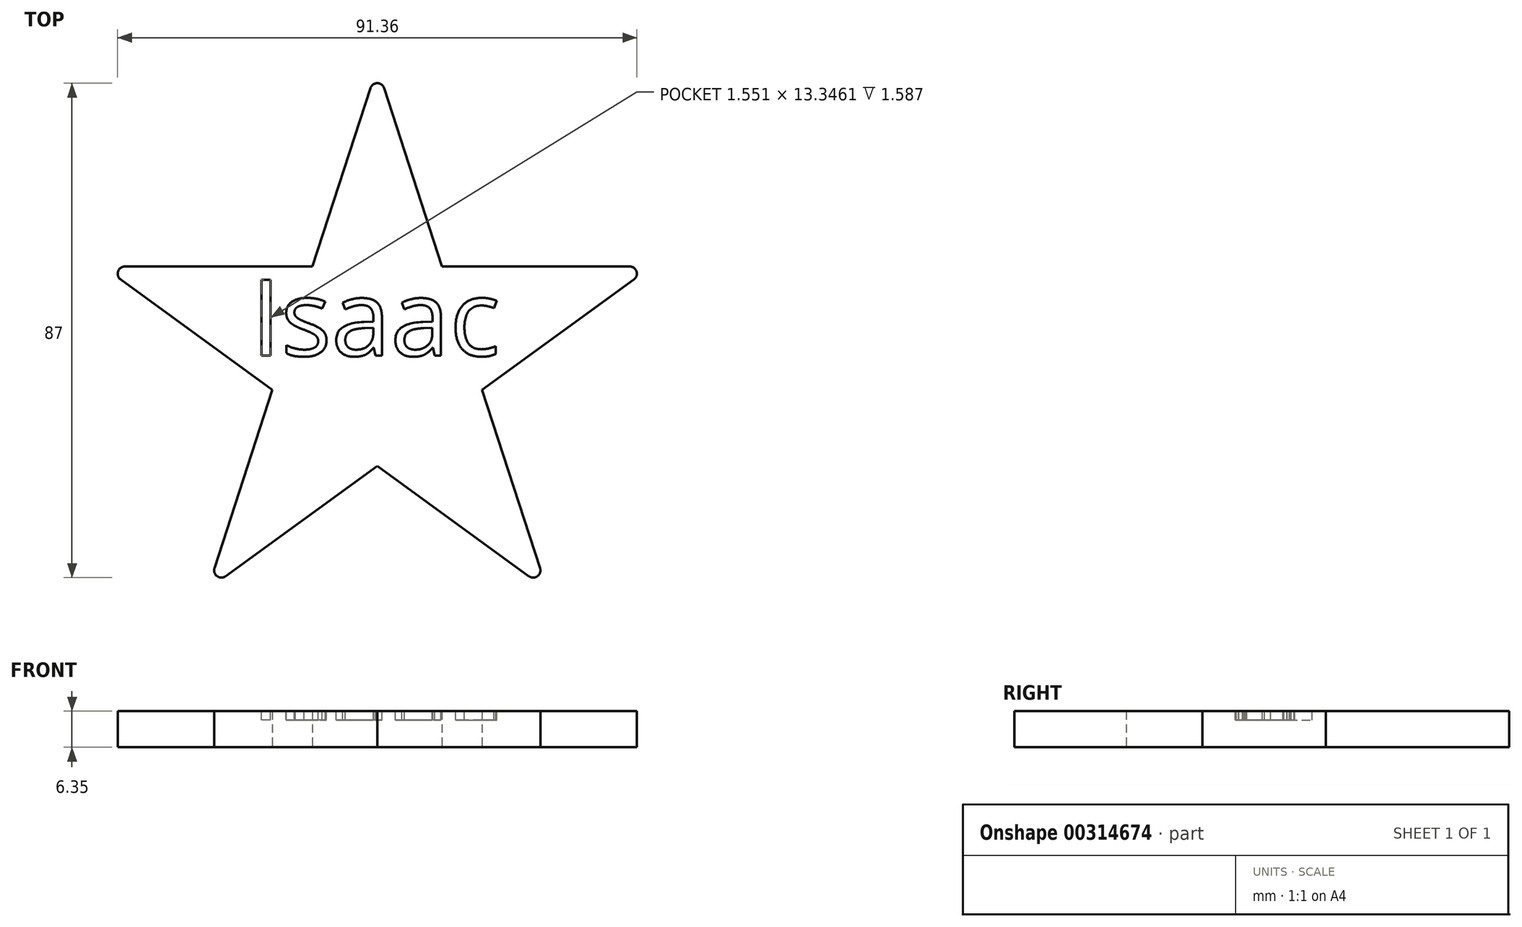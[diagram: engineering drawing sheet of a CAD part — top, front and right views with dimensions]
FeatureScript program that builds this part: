
annotation { "Feature Type Name" : "Feature", "Feature Type Description" : "" }
export const myFeature = defineFeature(function(context is Context, id is Id, definition is map)
    precondition{}
    {
        {
            var Q0;
            Q0=qCreatedBy(makeId("Top.planeOp"),FACE);
            var sketch = newSketch(context, id + "F0", { "sketchPlane" : qUnion([Q0])});
            skCircle(sketch, "E0.cCircle", {"center": v(0, 0) * mm, "radius": 50.8 * mm, "construction": true});
            skLineSegment(sketch, "E0.0", {"start": v(0, 50.8) * mm, "end": v(48.31, 15.7) * mm});
            skLineSegment(sketch, "E0.1", {"start": v(48.31, 15.7) * mm, "end": v(29.86, -41.1) * mm});
            skLineSegment(sketch, "E0.2", {"start": v(29.86, -41.1) * mm, "end": v(-29.86, -41.1) * mm});
            skLineSegment(sketch, "E0.3", {"start": v(-29.86, -41.1) * mm, "end": v(-48.31, 15.7) * mm});
            skLineSegment(sketch, "E0.4", {"start": v(-48.31, 15.7) * mm, "end": v(0, 50.8) * mm});
            skLineSegment(sketch, "E1", {"start": v(0, 50.8) * mm, "end": v(-29.86, -41.1) * mm});
            skLineSegment(sketch, "E2", {"start": v(0, 50.8) * mm, "end": v(29.86, -41.1) * mm});
            skLineSegment(sketch, "E3", {"start": v(-48.31, 15.7) * mm, "end": v(48.31, 15.7) * mm});
            skLineSegment(sketch, "E4", {"start": v(-48.31, 15.7) * mm, "end": v(29.86, -41.1) * mm});
            skLineSegment(sketch, "E5", {"start": v(48.31, 15.7) * mm, "end": v(-29.86, -41.1) * mm});
            skSolve(sketch);
        }
        {
            var Q0;
            {var subQ1=sQuery(id+"F0.wireOp",EDGE,"E1");var subQ3=sQuery(id+"F0.wireOp",EDGE,"E4");var subQ4=makeQuery(id+"F0.imprint","INTERSECT",VERTEX,{"derivedFrom":[subQ1,subQ3]});Q0=makeQuery(id+"F0.imprint","IMPRINT",FACE,{"disambiguationData":[TD([[makeQuery(id+"F0.imprint","IMPRINT",EDGE,{"disambiguationData":[TD([[subQ4,-1.0]])],"derivedFrom":subQ3}),-1.0]])]});}
            var Q1;
            {var subQ0=sQuery(id+"F0.wireOp",EDGE,"E3");var subQ1=sQuery(id+"F0.wireOp",EDGE,"E1");var subQ2=makeQuery(id+"F0.imprint","INTERSECT",VERTEX,{"derivedFrom":[subQ1,subQ0]});Q1=makeQuery(id+"F0.imprint","IMPRINT",FACE,{"disambiguationData":[TD([[makeQuery(id+"F0.imprint","IMPRINT",EDGE,{"disambiguationData":[TD([[subQ2,-1.0]])],"derivedFrom":subQ1}),-1.0]])]});}
            var Q2;
            {var subQ1=sQuery(id+"F0.wireOp",EDGE,"E1");var subQ3=sQuery(id+"F0.wireOp",EDGE,"E3");var subQ4=makeQuery(id+"F0.imprint","INTERSECT",VERTEX,{"derivedFrom":[subQ1,subQ3]});Q2=makeQuery(id+"F0.imprint","IMPRINT",FACE,{"disambiguationData":[TD([[makeQuery(id+"F0.imprint","IMPRINT",EDGE,{"disambiguationData":[TD([[subQ4,-1.0]])],"derivedFrom":subQ3}),1.0]])]});}
            var Q3;
            {var subQ1=sQuery(id+"F0.wireOp",EDGE,"E1");var subQ5=sQuery(id+"F0.wireOp",EDGE,"E3");var subQ6=makeQuery(id+"F0.imprint","INTERSECT",VERTEX,{"derivedFrom":[subQ1,subQ5]});Q3=makeQuery(id+"F0.imprint","IMPRINT",FACE,{"disambiguationData":[TD([[makeQuery(id+"F0.imprint","IMPRINT",EDGE,{"disambiguationData":[TD([[subQ6,-1.0]])],"derivedFrom":subQ1}),1.0]])]});}
            var Q4;
            {var subQ0=sQuery(id+"F0.wireOp",EDGE,"E3");var subQ1=sQuery(id+"F0.wireOp",EDGE,"E2");var subQ2=makeQuery(id+"F0.imprint","INTERSECT",VERTEX,{"derivedFrom":[subQ1,subQ0]});Q4=makeQuery(id+"F0.imprint","IMPRINT",FACE,{"disambiguationData":[TD([[makeQuery(id+"F0.imprint","IMPRINT",EDGE,{"disambiguationData":[TD([[subQ2,-1.0]])],"derivedFrom":subQ1}),1.0]])]});}
            var Q5;
            {var subQ1=sQuery(id+"F0.wireOp",EDGE,"E2");var subQ3=sQuery(id+"F0.wireOp",EDGE,"E5");var subQ4=makeQuery(id+"F0.imprint","INTERSECT",VERTEX,{"derivedFrom":[subQ1,subQ3]});Q5=makeQuery(id+"F0.imprint","IMPRINT",FACE,{"disambiguationData":[TD([[makeQuery(id+"F0.imprint","IMPRINT",EDGE,{"disambiguationData":[TD([[subQ4,-1.0]])],"derivedFrom":subQ3}),1.0]])]});}
            extrude(context, id + "F1", {"entities" : qUnion([Q0, Q1, Q2, Q3, Q4, Q5]), "depth" : 6.35 * mm});
        }
        {
            var Q0;
            Q0=makeQuery(id+"F1.opExtrude","SWEPT_EDGE",EDGE,{"disambiguationData":[OSD([sQuery(id+"F0.wireOp",EDGE,"E0.2"),sQuery(id+"F0.wireOp",EDGE,"E0.3"),sQuery(id+"F0.wireOp",EDGE,"E1"),sQuery(id+"F0.wireOp",EDGE,"E5")])]});
            var Q1;
            Q1=makeQuery(id+"F1.opExtrude","SWEPT_EDGE",EDGE,{"disambiguationData":[OSD([sQuery(id+"F0.wireOp",EDGE,"E0.1"),sQuery(id+"F0.wireOp",EDGE,"E0.2"),sQuery(id+"F0.wireOp",EDGE,"E2"),sQuery(id+"F0.wireOp",EDGE,"E4")])]});
            var Q2;
            Q2=makeQuery(id+"F1.opExtrude","SWEPT_EDGE",EDGE,{"disambiguationData":[OSD([sQuery(id+"F0.wireOp",EDGE,"E0.0"),sQuery(id+"F0.wireOp",EDGE,"E0.1"),sQuery(id+"F0.wireOp",EDGE,"E3"),sQuery(id+"F0.wireOp",EDGE,"E5")])]});
            var Q3;
            Q3=makeQuery(id+"F1.opExtrude","SWEPT_EDGE",EDGE,{"disambiguationData":[OSD([sQuery(id+"F0.wireOp",EDGE,"E0.0"),sQuery(id+"F0.wireOp",EDGE,"E0.4"),sQuery(id+"F0.wireOp",EDGE,"E1"),sQuery(id+"F0.wireOp",EDGE,"E2")])]});
            var Q4;
            Q4=makeQuery(id+"F1.opExtrude","SWEPT_EDGE",EDGE,{"disambiguationData":[OSD([sQuery(id+"F0.wireOp",EDGE,"E0.3"),sQuery(id+"F0.wireOp",EDGE,"E0.4"),sQuery(id+"F0.wireOp",EDGE,"E3"),sQuery(id+"F0.wireOp",EDGE,"E4")])]});
            fillet(context, id + "F2", {"entities" : qUnion([Q0, Q1, Q2, Q3, Q4]), "radius" : 1.27 * mm, "tangentPropagation" : true, "allowEdgeOverflow" : false});
        }
        {
            var Q0;
            Q0=makeQuery(id+"F1.opExtrude","CAP_FACE",FACE,{"disambiguationData":[OSD([sQuery(id+"F0.wireOp",EDGE,"E1"),sQuery(id+"F0.wireOp",EDGE,"E2"),sQuery(id+"F0.wireOp",EDGE,"E3"),sQuery(id+"F0.wireOp",EDGE,"E4"),sQuery(id+"F0.wireOp",EDGE,"E5")])],"isStart":false});
            var sketch = newSketch(context, id + "F3", { "sketchPlane" : qUnion([Q0])});
            skText(sketch, "E6", { "text": "Isaac", "fontName": "OpenSans-Regular.ttf"});
            const initialGuessF3  = {"E6": [-0.0222, 0, 1, 0, 0.01346]};
            skSetInitialGuess(sketch, initialGuessF3);
            skSolve(sketch);
        }
        {
            var Q0;
            Q0=makeQuery(id+"F3.imprint","IMPRINT",FACE,{"disambiguationData":[TD([[makeQuery(id+"F3.imprint","IMPRINT",EDGE,{"derivedFrom":sQuery(id+"F3.wireOp",EDGE,"E6.sketch_text.stroke-29")}),-1.0]])]});
            var Q1;
            Q1=makeQuery(id+"F3.imprint","IMPRINT",FACE,{"disambiguationData":[TD([[makeQuery(id+"F3.imprint","IMPRINT",EDGE,{"derivedFrom":sQuery(id+"F3.wireOp",EDGE,"E6.sketch_text.stroke-4")}),-1.0]])]});
            var Q2;
            Q2=makeQuery(id+"F3.imprint","IMPRINT",FACE,{"disambiguationData":[TD([[makeQuery(id+"F3.imprint","IMPRINT",EDGE,{"derivedFrom":sQuery(id+"F3.wireOp",EDGE,"E6.sketch_text.stroke-0")}),-1.0]])]});
            var Q3;
            Q3=makeQuery(id+"F3.imprint","IMPRINT",FACE,{"disambiguationData":[TD([[makeQuery(id+"F3.imprint","IMPRINT",EDGE,{"derivedFrom":sQuery(id+"F3.wireOp",EDGE,"E6.sketch_text.stroke-56")}),-1.0]])]});
            var Q4;
            Q4=makeQuery(id+"F3.imprint","IMPRINT",FACE,{"disambiguationData":[TD([[makeQuery(id+"F3.imprint","IMPRINT",EDGE,{"derivedFrom":sQuery(id+"F3.wireOp",EDGE,"E6.sketch_text.stroke-83")}),-1.0]])]});
            extrude(context, id + "F4", {"entities" : qUnion([Q0, Q1, Q2, Q3, Q4]), "operationType" : NewBodyOperationType.REMOVE, "oppositeDirection" : true, "depth" : 1.59 * mm});
        }
    });
